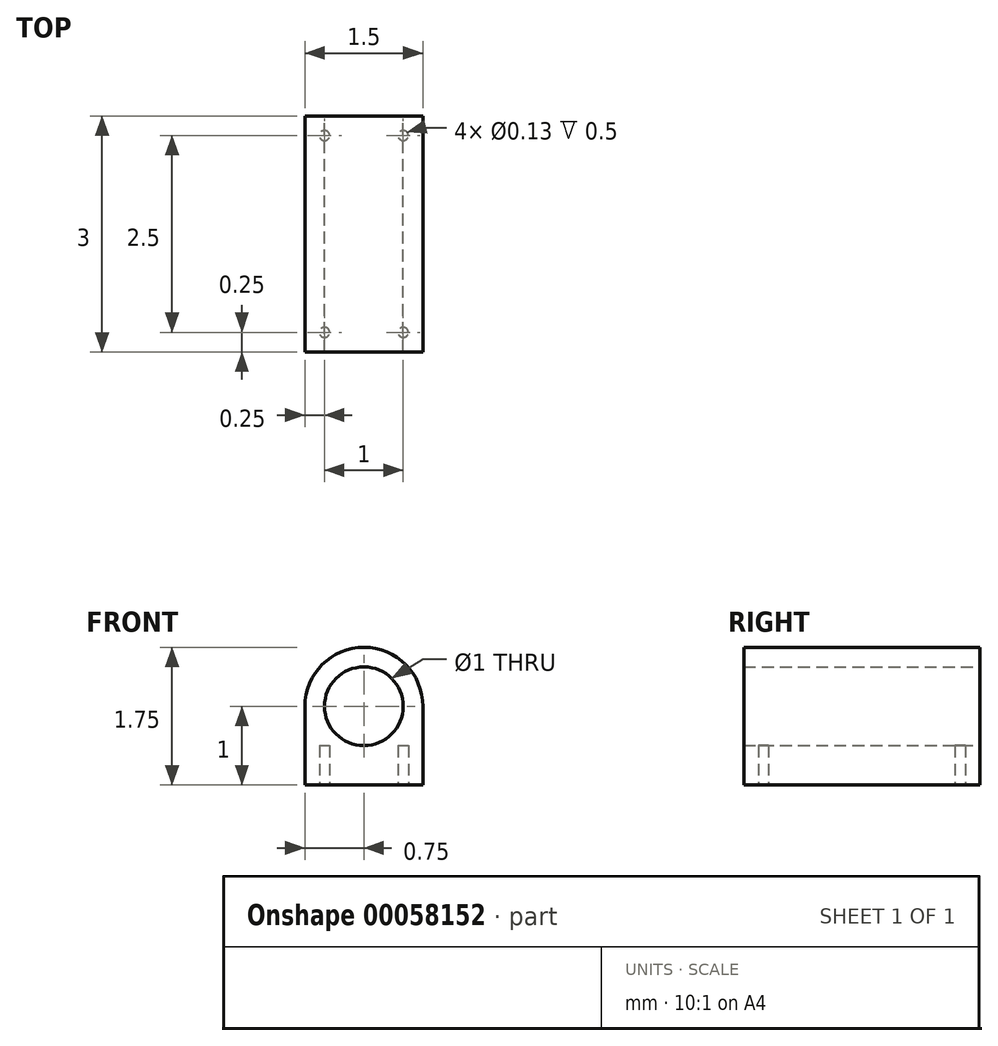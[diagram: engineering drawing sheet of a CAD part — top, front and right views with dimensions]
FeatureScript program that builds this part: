
annotation { "Feature Type Name" : "Feature", "Feature Type Description" : "" }
export const myFeature = defineFeature(function(context is Context, id is Id, definition is map)
    precondition{}
    {
        {
            var Q0;
            Q0=qCreatedBy(makeId("Front.planeOp"),FACE);
            var sketch = newSketch(context, id + "F0", { "sketchPlane" : qUnion([Q0])});
            skLineSegment(sketch, "E0", {"start": v(0, 0) * mm, "end": v(-0.75, 0) * mm});
            skLineSegment(sketch, "E1", {"start": v(-0.75, 0) * mm, "end": v(-0.75, 1) * mm});
            skArc(sketch, "E2", {"start": v(0, 1.75) * mm, "mid": v(-0.53, 1.53) * mm, "end": v(-0.75, 1) * mm});
            skCircle(sketch, "E3", {"center": v(0, 1) * mm, "radius": 0.5 * mm});
            skLineSegment(sketch, "E4.MirrorCS", {"start": v(0.75, 0) * mm, "end": v(0.75, 1) * mm});
            skLineSegment(sketch, "E5.MirrorCS", {"start": v(0, 0) * mm, "end": v(0.75, 0) * mm});
            skArc(sketch, "E6.MirrorCS", {"start": v(0, 1.75) * mm, "mid": v(0.53, 1.53) * mm, "end": v(0.75, 1) * mm});
            skSolve(sketch);
        }
        {
            var Q0;
            Q0=makeQuery(id+"F0.imprint","IMPRINT",FACE,{"disambiguationData":[TD([[makeQuery(id+"F0.imprint","IMPRINT",EDGE,{"derivedFrom":sQuery(id+"F0.wireOp",EDGE,"E0")}),-1.0]])]});
            extrude(context, id + "F1", {"entities" : qUnion([Q0]), "endBound" : BoundingType.SYMMETRIC, "depth" : 3 * mm});
        }
        {
            var Q0;
            Q0=makeQuery(id+"F1.opExtrude","SWEPT_FACE",FACE,{"disambiguationData":[OSD([sQuery(id+"F0.wireOp",EDGE,"E0"),sQuery(id+"F0.wireOp",EDGE,"E5.MirrorCS")])]});
            var sketch = newSketch(context, id + "F2", { "sketchPlane" : qUnion([Q0])});
            skCircle(sketch, "E7", {"center": v(-0.5, 1.25) * mm, "radius": 0.07 * mm});
            skCircle(sketch, "E8.MirrorC", {"center": v(0.5, 1.25) * mm, "radius": 0.07 * mm});
            skCircle(sketch, "E9.MirrorC", {"center": v(0.5, -1.25) * mm, "radius": 0.07 * mm});
            skCircle(sketch, "E10.MirrorC", {"center": v(-0.5, -1.25) * mm, "radius": 0.07 * mm});
            skSolve(sketch);
        }
        {
            var Q0;
            Q0 = qSketchRegion(id + "F2", true);
            extrude(context, id + "F3", {"entities" : qUnion([Q0]), "operationType" : NewBodyOperationType.REMOVE, "oppositeDirection" : true, "depth" : 0.5 * mm});
        }
    });
